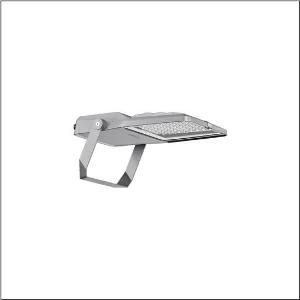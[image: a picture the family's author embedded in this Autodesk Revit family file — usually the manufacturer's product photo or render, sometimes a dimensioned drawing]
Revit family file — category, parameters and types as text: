
# Revit family: floodlight_fl_21_iq_mini___pl61_5xa7772d5c1a_2039
name_source: partatom
category: Lighting Fixtures
units: mm (PartAtom-declared; Revit-internal decimal feet)

## family parameters
Cut with Voids When Loaded = No
Host = Face
Light Source = No
Part Type = Normal
Room Calculation Point = No
Round Connector Dimension = Use Diameter
Shared = No

## types (1)
- --- (1 x LED, 16340 lm, 143 W, 4000K)
    Apparent Load = 143 VA
    CIE Flux Codes = 33 65 98 100 100
    Color Rendering = 80
    Color Temperature = 4000K
    Default Elevation = 1800 mm
    Description = Floodlight FL 21 iQ mini, floodlight, primary light control with lens, of PMMA, primary optical cover: protective disc, of toughened safety glass, transparent, light distribution: PL61, light emission: direct distribution, installation type: surface-mounted, LED, High Power LED, rated luminous flux: 16.340lm, luminous efficacy: 114lm/W, light colour: 840, colour temperature: 4000K, control: Street-Remote, Auto-Match, Temp-Guard, Night-Set, Smart-Wire, Desk-Remote (wireless, voltage-free reading and setting of iQ features in the workshop via application-optimized NFC function/RFID function), optimised constant luminous flux control (CLO 2.0), with terminal, 6-pole, mains connection: 220..240V, AC, 50/60Hz, start of lifetime: 143W, end of service life: 152W, reduction: 61W, luminaire housing, of diecast aluminium, powder-coated, Siteco® metallic grey (DB 702S), corrosivity category C5 mid according to DIN EN ISO 12944, sealing non-destructively replaceable, mounting bracket, of steel, galvanised, powder-coated, Siteco® metallic grey (DB 702S), protection rating (complete): IP66, insulation class (complete): insulation class II (safety insulation), certification: CE, ENEC, VDE, protection symbol: D, impact resistance: IK08, permissible operating ambient temperature: -40..+40°C, permissible operating ambient temperature for outdoor applications: -40..+50°C, standard: DIN EN 12944, LABS conformity tested according to VDMA 24364:2018-05, packaging unit: 1 piece

Light Distribution: PL61
    Height = 70 mm
    Lamp = 1 x LED
    Lamp Light Flux = 16340 lm
    Lamp Power = 143 W
    Lamp count = 1
    Length = 485 mm
    Luminous efficacy = 114 lm/W
    Manufacturer = Siteco
    ModVariant = No
    Model = 5XA7772D5C1A
    Number of Poles = 1
    OnlyDefault = Yes
    Power Factor = 1
    Product Name = Floodlight FL 21 iQ mini | PL61
    Product group = floodlight | pylon annexe
    ProductGroupID = 6200
    Protection Class = Protection class II
    Protection Degree = IP 66
    RLX_Detail_Level = 1
    RLX_Emergency_Light_Flux = 0 lm
    RLX_Emergency_Type = 0
    RLX_Emergency_Type_DB = No
    RlxData = <blob elided: 96437 chars, md5=9a6ec146>
    Socket = socket
    Standby Power = 0 W
    System Light Flux = 16340 lm
    System Power = 143 W
    Type Comments = factory setting: luminous flux: 100 % | dim-lin: 254 | 730 mA
    Type Image = l_1006845.jpg
    URL = http://relux.com
    VarID = @adj_105337
    Voltage = 0 V
    Weight = 0.00 kg
    Width = 337 mm

## geometry (parser evidence)
native form markers: Blend x4, Sweep x12
no freeform markers — native parametric forms only
